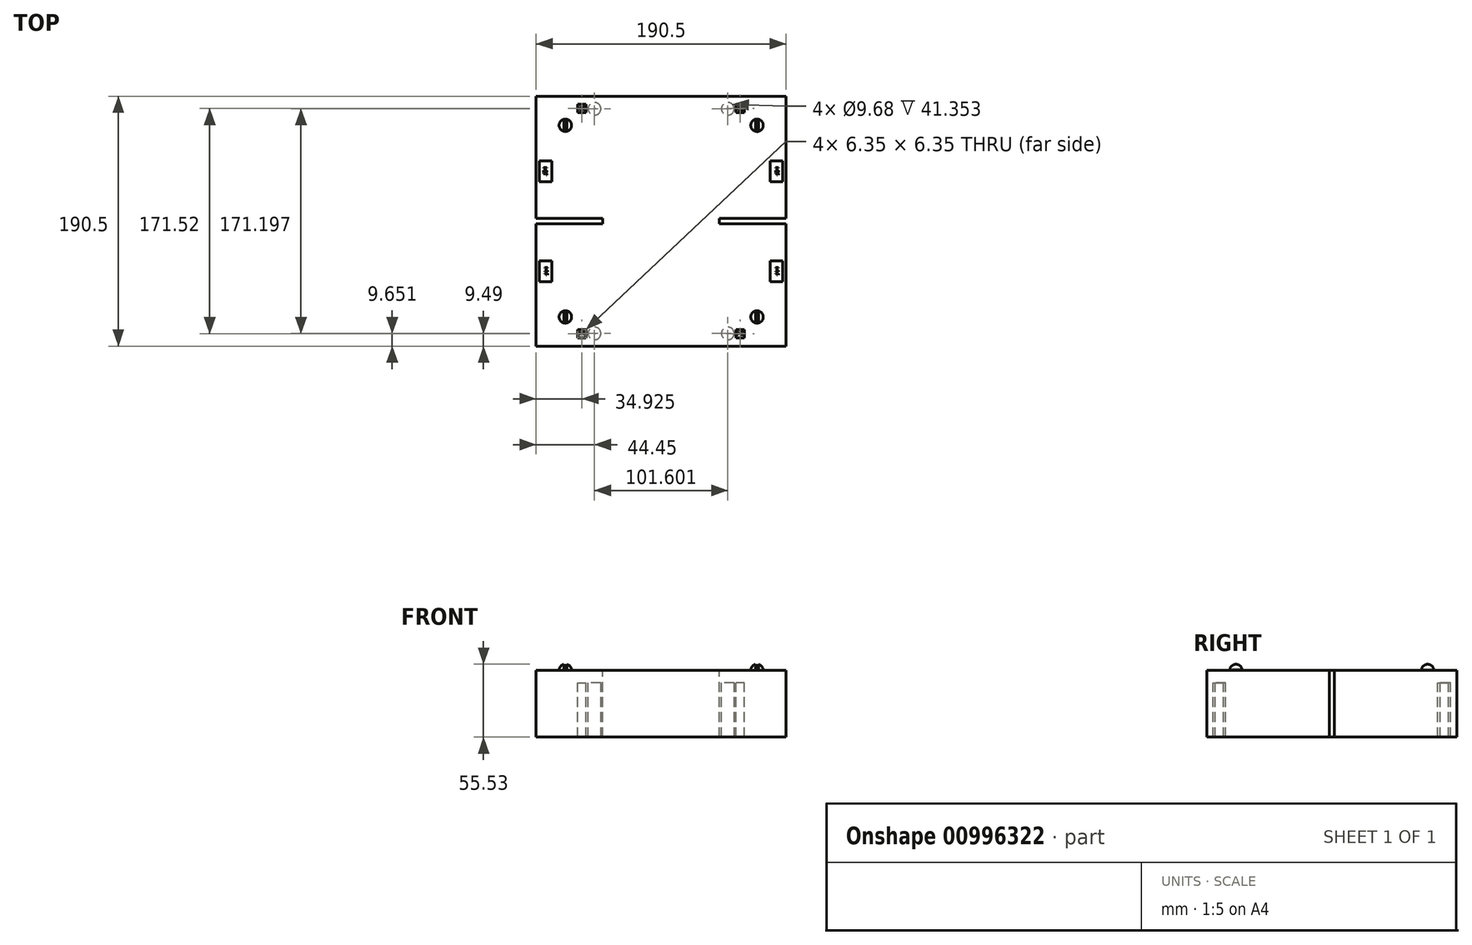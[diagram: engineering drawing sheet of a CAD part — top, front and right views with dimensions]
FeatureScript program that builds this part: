
annotation { "Feature Type Name" : "Feature", "Feature Type Description" : "" }
export const myFeature = defineFeature(function(context is Context, id is Id, definition is map)
    precondition{}
    {
        {
            var Q0;
            Q0=qCreatedBy(makeId("Top.planeOp"),FACE);
            var sketch = newSketch(context, id + "F0", { "sketchPlane" : qUnion([Q0])});
            skLineSegment(sketch, "E0.bottom", {"start": v(-95.25, 95.25) * mm, "end": v(95.25, 95.25) * mm});
            skLineSegment(sketch, "E0.top", {"start": v(-95.25, -95.25) * mm, "end": v(95.25, -95.25) * mm});
            skLineSegment(sketch, "E0.left", {"start": v(-95.25, 95.25) * mm, "end": v(-95.25, -95.25) * mm});
            skLineSegment(sketch, "E0.right", {"start": v(95.25, 95.25) * mm, "end": v(95.25, -95.25) * mm});
            skPoint(sketch, "E0.middle", {"position": v(0, 0) * mm});
            skLineSegment(sketch, "E1.bottom", {"start": v(95.25, 1.98) * mm, "end": v(44.45, 1.98) * mm});
            skLineSegment(sketch, "E1.top", {"start": v(95.25, -1.98) * mm, "end": v(44.45, -1.98) * mm});
            skLineSegment(sketch, "E1.left", {"start": v(95.25, 1.98) * mm, "end": v(95.25, -1.98) * mm});
            skLineSegment(sketch, "E1.right", {"start": v(44.45, 1.98) * mm, "end": v(44.45, -1.98) * mm});
            skLineSegment(sketch, "E2", {"start": v(0, 95.25) * mm, "end": v(0, 107.7) * mm, "construction": true});
            skLineSegment(sketch, "E3.MirrorCS", {"start": v(-95.25, 1.98) * mm, "end": v(-95.25, -1.98) * mm});
            skLineSegment(sketch, "E4.MirrorCS", {"start": v(-44.45, 1.98) * mm, "end": v(-44.45, -1.98) * mm});
            skLineSegment(sketch, "E5.MirrorCS", {"start": v(-95.25, 1.98) * mm, "end": v(-44.45, 1.98) * mm});
            skLineSegment(sketch, "E6.MirrorCS", {"start": v(-95.25, -1.98) * mm, "end": v(-44.45, -1.98) * mm});
            skSolve(sketch);
        }
        {
            var Q0;
            {var subQ3=sQuery(id+"F0.wireOp",EDGE,"E0.bottom");Q0=makeQuery(id+"F0.imprint","IMPRINT",FACE,{"disambiguationData":[TD([[makeQuery(id+"F0.imprint","IMPRINT",EDGE,{"derivedFrom":subQ3}),-1.0]])]});}
            extrude(context, id + "F1", {"entities" : qUnion([Q0]), "oppositeDirection" : true, "depth" : 9.53 * mm, "offsetDistance" : 25 * mm});
        }
        {
            var Q0;
            Q0=makeQuery(id+"F1.opExtrude","CAP_FACE",FACE,{"disambiguationData":[OSD([sQuery(id+"F0.wireOp",EDGE,"E0.bottom"),sQuery(id+"F0.wireOp",EDGE,"E0.top"),sQuery(id+"F0.wireOp",EDGE,"E0.left"),sQuery(id+"F0.wireOp",EDGE,"E0.right"),sQuery(id+"F0.wireOp",EDGE,"E1.bottom"),sQuery(id+"F0.wireOp",EDGE,"E1.top"),sQuery(id+"F0.wireOp",EDGE,"E1.right"),sQuery(id+"F0.wireOp",EDGE,"E4.MirrorCS"),sQuery(id+"F0.wireOp",EDGE,"E5.MirrorCS"),sQuery(id+"F0.wireOp",EDGE,"E6.MirrorCS")])],"isStart":true});
            var sketch = newSketch(context, id + "F2", { "sketchPlane" : qUnion([Q0])});
            skCircle(sketch, "E7", {"center": v(-73.03, -73.03) * mm, "radius": 4.76 * mm});
            skLineSegment(sketch, "E8", {"start": v(0, -95.25) * mm, "end": v(0, -109.98) * mm, "construction": true});
            skLineSegment(sketch, "E9", {"start": v(0, 0) * mm, "end": v(26.6, 0) * mm, "construction": true});
            skCircle(sketch, "E10.MirrorC", {"center": v(73.03, -73.03) * mm, "radius": 4.76 * mm});
            skCircle(sketch, "E11.MirrorC", {"center": v(-73.03, 73.03) * mm, "radius": 4.76 * mm});
            skCircle(sketch, "E12.MirrorC", {"center": v(73.03, 73.03) * mm, "radius": 4.76 * mm});
            skCircle(sketch, "E13", {"center": v(-50.8, 85.6) * mm, "radius": 4.84 * mm});
            skCircle(sketch, "E14.MirrorC", {"center": v(50.8, 85.6) * mm, "radius": 4.84 * mm});
            skCircle(sketch, "E15.MirrorC", {"center": v(50.8, -85.6) * mm, "radius": 4.84 * mm});
            skCircle(sketch, "E16.MirrorC", {"center": v(-50.8, -85.6) * mm, "radius": 4.84 * mm});
            skLineSegment(sketch, "E17.bottom", {"start": v(-63.5, 88.94) * mm, "end": v(-57.15, 88.94) * mm});
            skLineSegment(sketch, "E17.top", {"start": v(-63.5, 82.58) * mm, "end": v(-57.15, 82.58) * mm});
            skLineSegment(sketch, "E17.left", {"start": v(-63.5, 88.93) * mm, "end": v(-63.5, 82.58) * mm});
            skLineSegment(sketch, "E17.right", {"start": v(-57.15, 88.94) * mm, "end": v(-57.15, 82.58) * mm});
            skLineSegment(sketch, "E18.MirrorCS", {"start": v(63.5, 82.58) * mm, "end": v(57.15, 82.58) * mm});
            skLineSegment(sketch, "E19.MirrorCS", {"start": v(63.5, 88.93) * mm, "end": v(63.5, 82.58) * mm});
            skLineSegment(sketch, "E20.MirrorCS", {"start": v(57.15, 88.94) * mm, "end": v(57.15, 82.58) * mm});
            skLineSegment(sketch, "E21.MirrorCS", {"start": v(63.5, 88.94) * mm, "end": v(57.15, 88.94) * mm});
            skLineSegment(sketch, "E22.MirrorCS", {"start": v(-57.15, -88.93) * mm, "end": v(-57.15, -82.58) * mm});
            skLineSegment(sketch, "E23.MirrorCS", {"start": v(-63.5, -88.93) * mm, "end": v(-57.15, -88.93) * mm});
            skLineSegment(sketch, "E24.MirrorCS", {"start": v(-63.5, -82.58) * mm, "end": v(-57.15, -82.58) * mm});
            skLineSegment(sketch, "E25.MirrorCS", {"start": v(-63.5, -88.93) * mm, "end": v(-63.5, -82.58) * mm});
            skLineSegment(sketch, "E26.MirrorCS", {"start": v(63.5, -88.94) * mm, "end": v(57.15, -88.94) * mm});
            skLineSegment(sketch, "E27.MirrorCS", {"start": v(63.5, -88.94) * mm, "end": v(63.5, -82.58) * mm});
            skLineSegment(sketch, "E28.MirrorCS", {"start": v(57.15, -88.94) * mm, "end": v(57.15, -82.58) * mm});
            skLineSegment(sketch, "E29.MirrorCS", {"start": v(63.5, -82.58) * mm, "end": v(57.15, -82.58) * mm});
            skText(sketch, "E30", { "text": "X1", "fontName": "OpenSans-Regular.ttf"});
            skText(sketch, "E31", { "text": "X2\n", "fontName": "OpenSans-Regular.ttf"});
            skText(sketch, "E32", { "text": "H1\n", "fontName": "OpenSans-Regular.ttf"});
            skText(sketch, "E33", { "text": "H2\n\n", "fontName": "OpenSans-Regular.ttf"});
            const initialGuessF2  = {"E30": [-0.0622, 0.08438, 1, 0, 0.00274], "E31": [0.05845, 0.08438, 1, 0, 0.00274], "E32": [-0.0622, -0.08662, 1, 0, 0.00224], "E33": [0.05805, -0.08662, 1, 0, 0.00224]};
            skSetInitialGuess(sketch, initialGuessF2);
            skSolve(sketch);
        }
        {
            var Q0;
            Q0=makeQuery(id+"F2.imprint","IMPRINT",FACE,{"disambiguationData":[TD([[makeQuery(id+"F2.imprint","IMPRINT",EDGE,{"derivedFrom":sQuery(id+"F2.wireOp",EDGE,"E13")}),1.0]])]});
            var Q1;
            Q1=makeQuery(id+"F2.imprint","IMPRINT",FACE,{"disambiguationData":[TD([[makeQuery(id+"F2.imprint","IMPRINT",EDGE,{"derivedFrom":sQuery(id+"F2.wireOp",EDGE,"E14.MirrorC")}),-1.0]])]});
            var Q2;
            Q2=makeQuery(id+"F2.imprint","IMPRINT",FACE,{"disambiguationData":[TD([[makeQuery(id+"F2.imprint","IMPRINT",EDGE,{"derivedFrom":sQuery(id+"F2.wireOp",EDGE,"E16.MirrorC")}),-1.0]])]});
            var Q3;
            Q3=makeQuery(id+"F2.imprint","IMPRINT",FACE,{"disambiguationData":[TD([[makeQuery(id+"F2.imprint","IMPRINT",EDGE,{"derivedFrom":sQuery(id+"F2.wireOp",EDGE,"E15.MirrorC")}),1.0]])]});
            extrude(context, id + "F3", {"entities" : qUnion([Q0, Q1, Q2, Q3]), "operationType" : NewBodyOperationType.REMOVE, "oppositeDirection" : true, "depth" : 25 * mm, "offsetDistance" : 25 * mm});
        }
        {
            var Q0;
            Q0=makeQuery(id+"F1.opExtrude","CAP_FACE",FACE,{"disambiguationData":[OSD([sQuery(id+"F0.wireOp",EDGE,"E0.bottom"),sQuery(id+"F0.wireOp",EDGE,"E0.top"),sQuery(id+"F0.wireOp",EDGE,"E0.left"),sQuery(id+"F0.wireOp",EDGE,"E0.right"),sQuery(id+"F0.wireOp",EDGE,"E1.bottom"),sQuery(id+"F0.wireOp",EDGE,"E1.top"),sQuery(id+"F0.wireOp",EDGE,"E1.right"),sQuery(id+"F0.wireOp",EDGE,"E4.MirrorCS"),sQuery(id+"F0.wireOp",EDGE,"E5.MirrorCS"),sQuery(id+"F0.wireOp",EDGE,"E6.MirrorCS")])],"isStart":true});
            var sketch = newSketch(context, id + "F4", { "sketchPlane" : qUnion([Q0])});
            skLineSegment(sketch, "E34.bottom", {"start": v(-92.7, 46.04) * mm, "end": v(-83.18, 46.04) * mm});
            skLineSegment(sketch, "E34.top", {"start": v(-92.7, 30.16) * mm, "end": v(-83.18, 30.16) * mm});
            skLineSegment(sketch, "E34.left", {"start": v(-92.7, 46.04) * mm, "end": v(-92.7, 30.16) * mm});
            skLineSegment(sketch, "E34.right", {"start": v(-83.18, 46.04) * mm, "end": v(-83.18, 30.16) * mm});
            skPoint(sketch, "E35.0", {"position": v(0, 95.25) * mm});
            skPoint(sketch, "E36.0", {"position": v(-44.45, 0) * mm});
            skLineSegment(sketch, "E37", {"start": v(0, 95.25) * mm, "end": v(0, 120.3) * mm, "construction": true});
            skLineSegment(sketch, "E38", {"start": v(-44.45, 0) * mm, "end": v(-55.95, 0) * mm, "construction": true});
            skLineSegment(sketch, "E39.MirrorCS", {"start": v(92.7, 46.04) * mm, "end": v(83.18, 46.04) * mm});
            skLineSegment(sketch, "E40.MirrorCS", {"start": v(92.7, 30.16) * mm, "end": v(83.18, 30.16) * mm});
            skLineSegment(sketch, "E41.MirrorCS", {"start": v(92.7, 46.04) * mm, "end": v(92.7, 30.16) * mm});
            skLineSegment(sketch, "E42.MirrorCS", {"start": v(83.18, 46.04) * mm, "end": v(83.18, 30.16) * mm});
            skLineSegment(sketch, "E43.MirrorCS", {"start": v(-92.7, -30.16) * mm, "end": v(-83.18, -30.16) * mm});
            skLineSegment(sketch, "E44.MirrorCS", {"start": v(-92.7, -46.04) * mm, "end": v(-83.18, -46.04) * mm});
            skLineSegment(sketch, "E45.MirrorCS", {"start": v(92.7, -46.04) * mm, "end": v(83.18, -46.04) * mm});
            skLineSegment(sketch, "E46.MirrorCS", {"start": v(92.7, -30.16) * mm, "end": v(83.18, -30.16) * mm});
            skLineSegment(sketch, "E47.MirrorCS", {"start": v(-83.18, -46.04) * mm, "end": v(-83.18, -30.16) * mm});
            skLineSegment(sketch, "E48.MirrorCS", {"start": v(92.7, -46.04) * mm, "end": v(92.7, -30.16) * mm});
            skLineSegment(sketch, "E49.MirrorCS", {"start": v(-92.7, -46.04) * mm, "end": v(-92.7, -30.16) * mm});
            skLineSegment(sketch, "E50.MirrorCS", {"start": v(83.18, -46.04) * mm, "end": v(83.18, -30.16) * mm});
            skText(sketch, "E51", { "text": "H2F", "fontName": "OpenSans-Regular.ttf"});
            skText(sketch, "E52", { "text": "H2F", "fontName": "OpenSans-Regular.ttf"});
            skText(sketch, "E53", { "text": "H1F", "fontName": "OpenSans-Regular.ttf"});
            skText(sketch, "E54", { "text": "H1F\n", "fontName": "OpenSans-Regular.ttf"});
            const initialGuessF4  = {"E51": [-0.08953, 0.04128, 0, -1, 0.00245], "E52": [0.08708, 0.04128, 0, -1, 0.00245], "E53": [-0.0888, -0.03492, 0, -1, 0.00245], "E54": [0.08708, -0.03492, 0, -1, 0.00245]};
            skSetInitialGuess(sketch, initialGuessF4);
            skSolve(sketch);
        }
        {
            var Q0;
            Q0=makeQuery(id+"F2.imprint","IMPRINT",FACE,{"disambiguationData":[TD([[makeQuery(id+"F2.imprint","IMPRINT",EDGE,{"derivedFrom":sQuery(id+"F2.wireOp",EDGE,"E11.MirrorC")}),-1.0]])]});
            var Q1;
            Q1=makeQuery(id+"F2.imprint","IMPRINT",FACE,{"disambiguationData":[TD([[makeQuery(id+"F2.imprint","IMPRINT",EDGE,{"derivedFrom":sQuery(id+"F2.wireOp",EDGE,"E7")}),1.0]])]});
            var Q2;
            Q2=makeQuery(id+"F2.imprint","IMPRINT",FACE,{"disambiguationData":[TD([[makeQuery(id+"F2.imprint","IMPRINT",EDGE,{"derivedFrom":sQuery(id+"F2.wireOp",EDGE,"E12.MirrorC")}),1.0]])]});
            var Q3;
            Q3=makeQuery(id+"F2.imprint","IMPRINT",FACE,{"disambiguationData":[TD([[makeQuery(id+"F2.imprint","IMPRINT",EDGE,{"derivedFrom":sQuery(id+"F2.wireOp",EDGE,"E10.MirrorC")}),-1.0]])]});
            extrude(context, id + "F5", {"entities" : qUnion([Q0, Q1, Q2, Q3]), "operationType" : NewBodyOperationType.ADD, "oppositeDirection" : true, "depth" : 50.88 * mm, "offsetDistance" : 25 * mm});
        }
        {
            var Q0;
            Q0=qCreatedBy(makeId("Front.planeOp"),FACE);
            cPlane(context, id + "F6", {"entities" : qUnion([Q0]), "cplaneType" : CPlaneType.OFFSET, "offset" : 73.03 * mm, "width" : 150 * mm, "height" : 150 * mm});
        }
        {
            var Q0;
            Q0=qCreatedBy(id+"F6.planeOp",FACE);
            var sketch = newSketch(context, id + "F7", { "sketchPlane" : qUnion([Q0])});
            skPoint(sketch, "E55.0", {"position": v(-73.03, 0) * mm});
            skLineSegment(sketch, "E56.0", {"start": v(-77.79, 0) * mm, "end": v(-68.26, 0) * mm});
            skLineSegment(sketch, "E57", {"start": v(-73.03, 0) * mm, "end": v(-73.03, 4.76) * mm});
            skArc(sketch, "E58", {"start": v(-68.26, 0) * mm, "mid": v(-69.66, 3.37) * mm, "end": v(-73.03, 4.76) * mm});
            skSolve(sketch);
        }
        {
            var Q0;
            {var subQ0=sQuery(id+"F7.wireOp",EDGE,"E57");Q0=makeQuery(id+"F7.imprint","IMPRINT",FACE,{"disambiguationData":[TD([[makeQuery(id+"F7.imprint","IMPRINT",EDGE,{"derivedFrom":subQ0}),-1.0]])]});}
            var Q1;
            Q1=sQuery(id+"F7.wireOp",EDGE,"E57");
            revolve(context, id + "F8", {"surfaceOperationType" : NewSurfaceOperationType.NEW, "entities" : qUnion([Q0]), "axis" : qUnion([Q1]), "revolveType" : RevolveType.FULL});
        }
        {
            var Q0;
            Q0=qCreatedBy(id+"F6.planeOp",FACE);
            var sketch = newSketch(context, id + "F9", { "sketchPlane" : qUnion([Q0])});
            skArc(sketch, "E59", {"start": v(-68.26, 0) * mm, "mid": v(-73.03, 4.76) * mm, "end": v(-77.79, 0) * mm});
            skLineSegment(sketch, "E60.bottom", {"start": v(-74.06, 5.91) * mm, "end": v(-71.99, 5.91) * mm});
            skLineSegment(sketch, "E60.top", {"start": v(-74.06, 1) * mm, "end": v(-71.99, 1) * mm});
            skLineSegment(sketch, "E60.left", {"start": v(-74.06, 5.91) * mm, "end": v(-74.06, 1) * mm});
            skLineSegment(sketch, "E60.right", {"start": v(-71.99, 5.91) * mm, "end": v(-71.99, 1) * mm});
            skPoint(sketch, "E61", {"position": v(-73.03, 1) * mm});
            skSolve(sketch);
        }
        {
            var Q0;
            Q0 = qSketchRegion(id + "F9", true);
            extrude(context, id + "F10", {"entities" : qUnion([Q0]), "operationType" : NewBodyOperationType.REMOVE, "endBound" : BoundingType.SYMMETRIC, "oppositeDirection" : true, "depth" : 25 * mm, "offsetDistance" : 25 * mm});
        }
        {
            var Q0;
            Q0=makeQuery(id+"F8.opRevolve","SWEPT_BODY",BODY,{"disambiguationData":[OSD([sQuery(id+"F7.wireOp",EDGE,"E56.0"),sQuery(id+"F7.wireOp",EDGE,"E57"),sQuery(id+"F7.wireOp",EDGE,"E58")])]});
            var Q1;
            Q1=qCreatedBy(makeId("Right.planeOp"),FACE);
            mirror(context, id + "F11", {"operationType" : NewBodyOperationType.ADD, "entities" : qUnion([Q0]), "mirrorPlane" : qUnion([Q1])});
        }
        {
            var Q0;
            Q0=makeQuery(id+"F1.opExtrude","SWEPT_BODY",BODY,{"disambiguationData":[OSD([sQuery(id+"F0.wireOp",EDGE,"E0.bottom"),sQuery(id+"F0.wireOp",EDGE,"E0.top"),sQuery(id+"F0.wireOp",EDGE,"E0.left"),sQuery(id+"F0.wireOp",EDGE,"E0.right"),sQuery(id+"F0.wireOp",EDGE,"E1.bottom"),sQuery(id+"F0.wireOp",EDGE,"E1.top"),sQuery(id+"F0.wireOp",EDGE,"E1.right"),sQuery(id+"F0.wireOp",EDGE,"E4.MirrorCS"),sQuery(id+"F0.wireOp",EDGE,"E5.MirrorCS"),sQuery(id+"F0.wireOp",EDGE,"E6.MirrorCS")])]});
            var Q1;
            Q1=qCreatedBy(makeId("Front.planeOp"),FACE);
            mirror(context, id + "F12", {"operationType" : NewBodyOperationType.ADD, "entities" : qUnion([Q0]), "mirrorPlane" : qUnion([Q1])});
        }
        {
            var Q0;
            Q0 = qSketchRegion(id + "F4", true);
            var Q1;
            Q1=makeQuery(id+"F2.imprint","IMPRINT",FACE,{"disambiguationData":[TD([[makeQuery(id+"F2.imprint","IMPRINT",EDGE,{"derivedFrom":sQuery(id+"F2.wireOp",EDGE,"E22.MirrorCS")}),1.0]])]});
            var Q2;
            Q2=makeQuery(id+"F2.imprint","IMPRINT",FACE,{"disambiguationData":[TD([[makeQuery(id+"F2.imprint","IMPRINT",EDGE,{"derivedFrom":sQuery(id+"F2.wireOp",EDGE,"E26.MirrorCS")}),-1.0]])]});
            var Q3;
            Q3=makeQuery(id+"F2.imprint","IMPRINT",FACE,{"disambiguationData":[TD([[makeQuery(id+"F2.imprint","IMPRINT",EDGE,{"derivedFrom":sQuery(id+"F2.wireOp",EDGE,"E18.MirrorCS")}),-1.0]])]});
            var Q4;
            Q4=makeQuery(id+"F2.imprint","IMPRINT",FACE,{"disambiguationData":[TD([[makeQuery(id+"F2.imprint","IMPRINT",EDGE,{"derivedFrom":sQuery(id+"F2.wireOp",EDGE,"E17.bottom")}),-1.0]])]});
            extrude(context, id + "F13", {"entities" : qUnion([Q0, Q1, Q2, Q3, Q4]), "operationType" : NewBodyOperationType.ADD, "depth" : 0.13 * mm, "offsetDistance" : 25 * mm});
        }
    });
